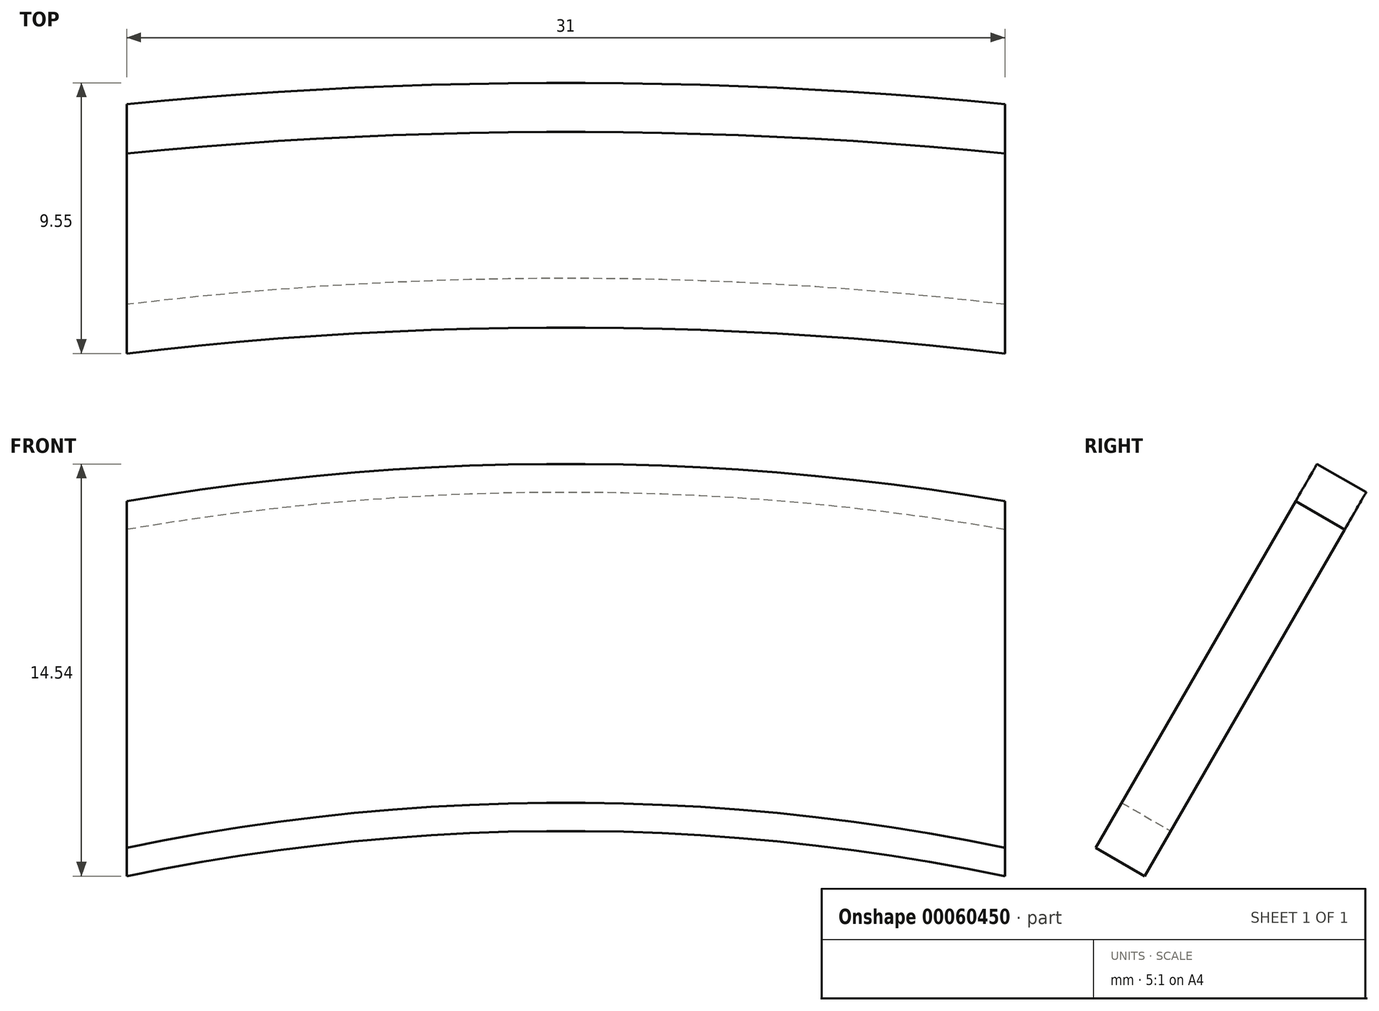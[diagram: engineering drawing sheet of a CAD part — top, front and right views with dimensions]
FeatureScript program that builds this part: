
annotation { "Feature Type Name" : "Feature", "Feature Type Description" : "" }
export const myFeature = defineFeature(function(context is Context, id is Id, definition is map)
    precondition{}
    {
        {
            var Q0;
            Q0=qCreatedBy(makeId("Front.planeOp"),FACE);
            var sketch = newSketch(context, id + "F0", { "sketchPlane" : qUnion([Q0])});
            skCircle(sketch, "E0", {"center": v(0, 0) * mm, "radius": 80 * mm});
            skCircle(sketch, "E1", {"center": v(0, 0) * mm, "radius": 66.2 * mm});
            skLineSegment(sketch, "E2", {"start": v(-15.5, 84.3) * mm, "end": v(-15.5, -48.7) * mm});
            skLineSegment(sketch, "E3", {"start": v(15.5, 85.15) * mm, "end": v(15.5, -45.48) * mm});
            skLineSegment(sketch, "E4", {"start": v(-86.44, 0) * mm, "end": v(88.19, 0) * mm, "construction": true});
            skSolve(sketch);
        }
        {
            var Q0;
            {var subQ0=sQuery(id+"F0.wireOp",EDGE,"E2");var subQ1=sQuery(id+"F0.wireOp",EDGE,"E0");var subQ2=makeQuery(id+"F0.imprint","INTERSECT",VERTEX,{"derivedFrom":[subQ1,subQ0]});Q0=makeQuery(id+"F0.imprint","IMPRINT",FACE,{"disambiguationData":[TD([[makeQuery(id+"F0.imprint","IMPRINT",EDGE,{"disambiguationData":[TD([[subQ2,1.0]])],"derivedFrom":subQ1}),1.0]])]});}
            extrude(context, id + "F1", {"entities" : qUnion([Q0]), "depth" : 2 * mm});
        }
        {
            var Q0;
            Q0=makeQuery(id+"F1.opExtrude","SWEPT_BODY",BODY,{"disambiguationData":[OSD([sQuery(id+"F0.wireOp",EDGE,"E0"),sQuery(id+"F0.wireOp",EDGE,"E1"),sQuery(id+"F0.wireOp",EDGE,"E2"),sQuery(id+"F0.wireOp",EDGE,"E3")])]});
            var Q1;
            Q1=sQuery(id+"F0.wireOp",EDGE,"E4");
            transform(context, id + "F2", {"entities" : qUnion([Q0]), "transformType" : TransformType.ROTATION, "transformAxis" : qUnion([Q1]), "angle" : 30 * degree, "oppositeDirection" : true, "makeCopy" : false});
        }
    });
